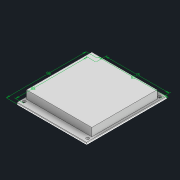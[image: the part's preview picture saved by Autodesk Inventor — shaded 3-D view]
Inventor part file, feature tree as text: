
AUTODESK INVENTOR PART (.ipt)
format: ipt  version: 2022 (Build 260153000, 153)  size: 98,816 bytes
history: native  units: mm
features: sketch x2, extrude x2, hole x1
ambient origin geometry x8: Origin, YZ Plane, XZ Plane, XY Plane, X Axis, Y Axis, Z Axis, Center Point
bodies: Solid1 (feature_tree)
feature tree (5):
  sketch  "Sketch1"  dims[d0=85.0mm d1=98.0mm]
  extrude  "Extrusion1"  Depth=98.0mm
  hole  "Hole1"  [1 undecoded]
  extrude  "Extrusion2"  Depth=2.0mm TaperAngle=0.0deg
  sketch  "Sketch2"  dims[d2=78.0mm d3=88.0mm d4=2.0mm d5=0.0mm d6=3.6mm d7=6.0mm d8=6.5mm d9=3.4mm d10=90.0deg d11=8.0mm d12=20.594885mm d13=80.0mm d14=80.0mm d15=10.0mm d16=0.0mm]
note: 1 required parameter value undecoded (feature->parameter linkage not recoverable at this tier; creation-order binding heuristic only, values carry confidence <= 0.55)
